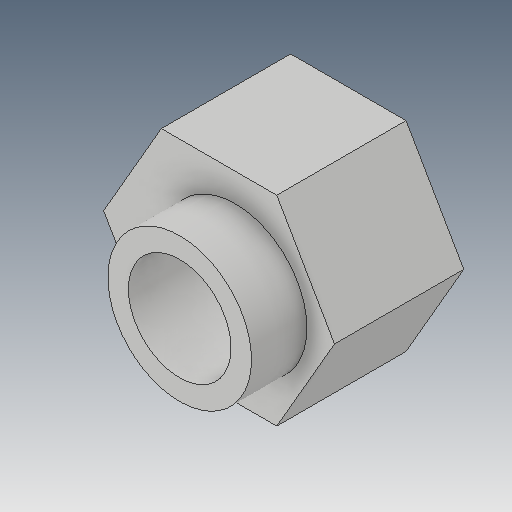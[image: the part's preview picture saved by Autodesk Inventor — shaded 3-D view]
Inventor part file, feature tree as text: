
AUTODESK INVENTOR PART (.ipt)
format: ipt  version: 2017 (Build 210142000, 142)  size: 127,488 bytes
history: native  units: mm
features: extrude x3, sketch x3, other x3, reference x1, projected_geometry x1
ambient origin geometry x8: Origin, YZ Plane, XZ Plane, XY Plane, X Axis, Y Axis, Z Axis, Center Point
bodies: Solid1 (feature_tree)
feature tree (11):
  extrude  "Extrusion1"  Depth=6.3mm TaperAngle=0.0deg
  extrude  "Extrusion2"  Depth=2.7mm TaperAngle=0.0deg
  extrude  "Extrusion3"  [1 undecoded]
  sketch  "Sketch1"  dims[d0=5.625mm d1=6.3mm d2=0.0mm]
  sketch  "Sketch2"  dims[d3=7.0mm d4=2.7mm d5=0.0mm]
  reference  "Reference2"
  sketch  "Sketch3"  dims[d6=2.7mm d7=0.0mm]
  projected_geometry  "Projected Loop1"
  other  "<userpath>\OneDrive\SL-Inventor\SL-Beast 3D Printer\DelrinY-Wheel-Bottom.iam"
  other  "DelrinY-Wheel-Bottom.iam"
  other  "Forged Socket Head Cap Screw - Metric M5x0.8 x 35:1"
note: 1 required parameter value undecoded (feature->parameter linkage not recoverable at this tier; creation-order binding heuristic only, values carry confidence <= 0.55)
